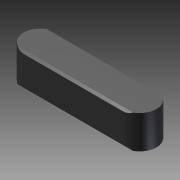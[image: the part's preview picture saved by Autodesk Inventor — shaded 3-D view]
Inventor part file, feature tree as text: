
AUTODESK INVENTOR PART (.ipt)
format: ipt  version: 2011 SP1 (Build 150282100, 282)  size: 86,016 bytes
history: native  units: mm
features: extrude x2, sketch x2
ambient origin geometry x8: Origin, YZ Plane, XZ Plane, XY Plane, X Axis, Y Axis, Z Axis, Center Point
bodies: Solid1 (feature_tree)
feature tree (4):
  extrude  "Extrusion1"  Depth=20.0mm TaperAngle=0.0deg
  extrude  "Extrusion2"  [1 undecoded]
  sketch  "Sketch_7"  dims[d0=5.0mm d1=0.0mm d2=20.0mm d3=0.0mm]
  sketch  "Sketch_8"
note: 1 required parameter value undecoded (feature->parameter linkage not recoverable at this tier; creation-order binding heuristic only, values carry confidence <= 0.55)
